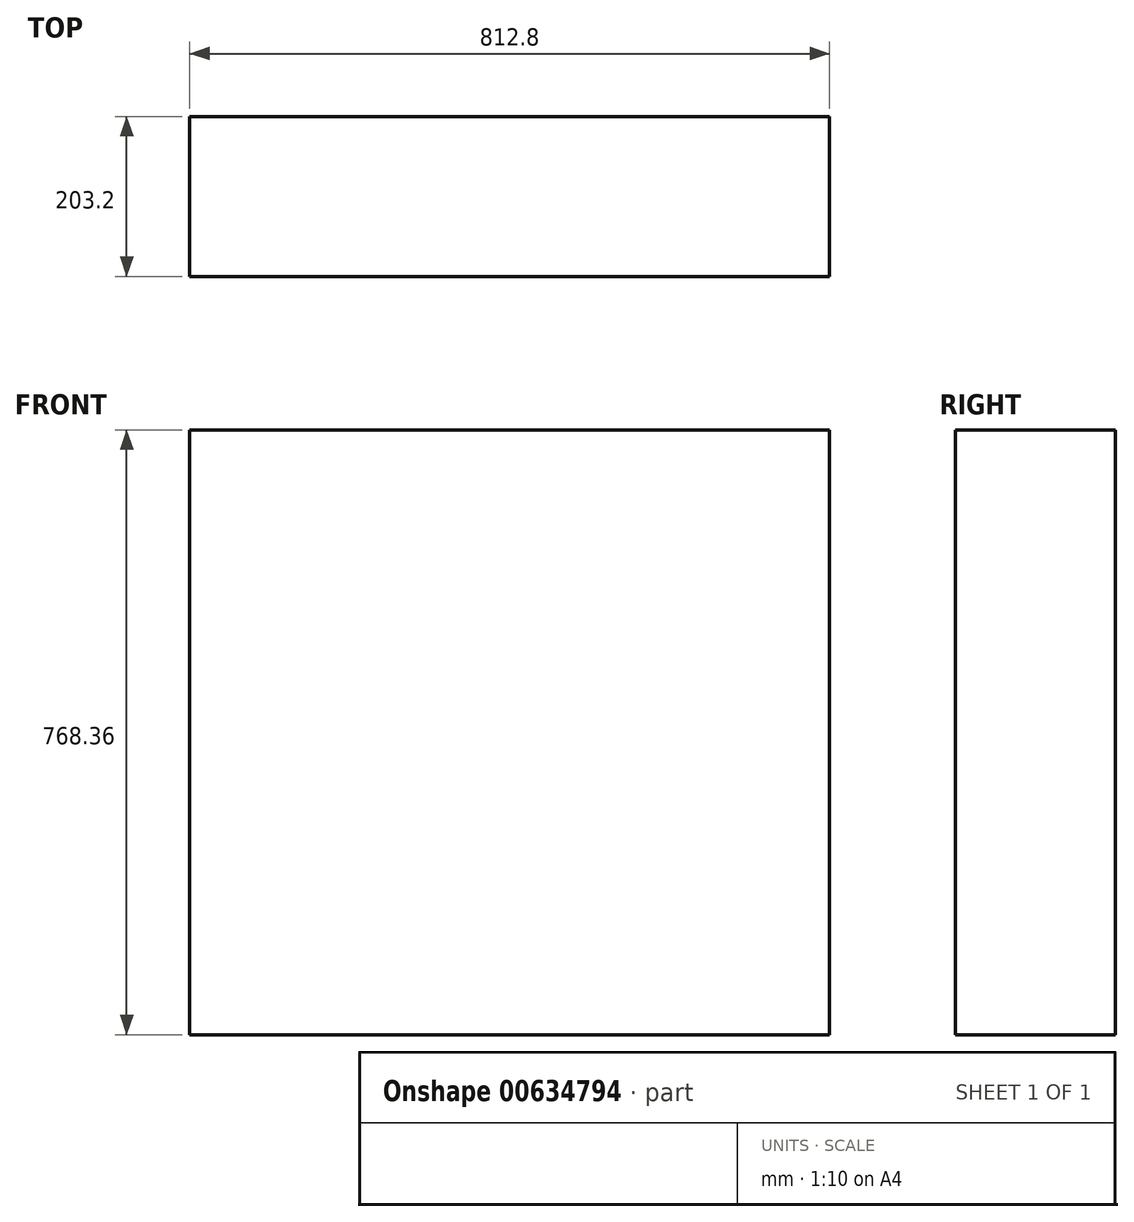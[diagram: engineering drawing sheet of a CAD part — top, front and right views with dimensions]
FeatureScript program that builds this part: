
annotation { "Feature Type Name" : "Feature", "Feature Type Description" : "" }
export const myFeature = defineFeature(function(context is Context, id is Id, definition is map)
    precondition{}
    {
        {
            var Q0;
            Q0=qCreatedBy(makeId("Right.planeOp"),FACE);
            var sketch = newSketch(context, id + "F0", { "sketchPlane" : qUnion([Q0])});
            skLineSegment(sketch, "E0.bottom", {"start": v(-101.6, 384.18) * mm, "end": v(101.6, 384.18) * mm});
            skLineSegment(sketch, "E0.top", {"start": v(-101.6, -384.18) * mm, "end": v(101.6, -384.18) * mm});
            skLineSegment(sketch, "E0.left", {"start": v(-101.6, 384.18) * mm, "end": v(-101.6, -384.18) * mm});
            skLineSegment(sketch, "E0.right", {"start": v(101.6, 384.18) * mm, "end": v(101.6, -384.18) * mm});
            skLineSegment(sketch, "E1", {"start": v(101.6, 384.18) * mm, "end": v(-101.6, -384.18) * mm, "construction": true});
            skSolve(sketch);
        }
        {
            var Q0;
            Q0 = qSketchRegion(id + "F0", true);
            extrude(context, id + "F1", {"entities" : qUnion([Q0]), "endBound" : BoundingType.SYMMETRIC, "depth" : 812.8 * mm, "offsetDistance" : 25.4 * mm});
        }
    });
